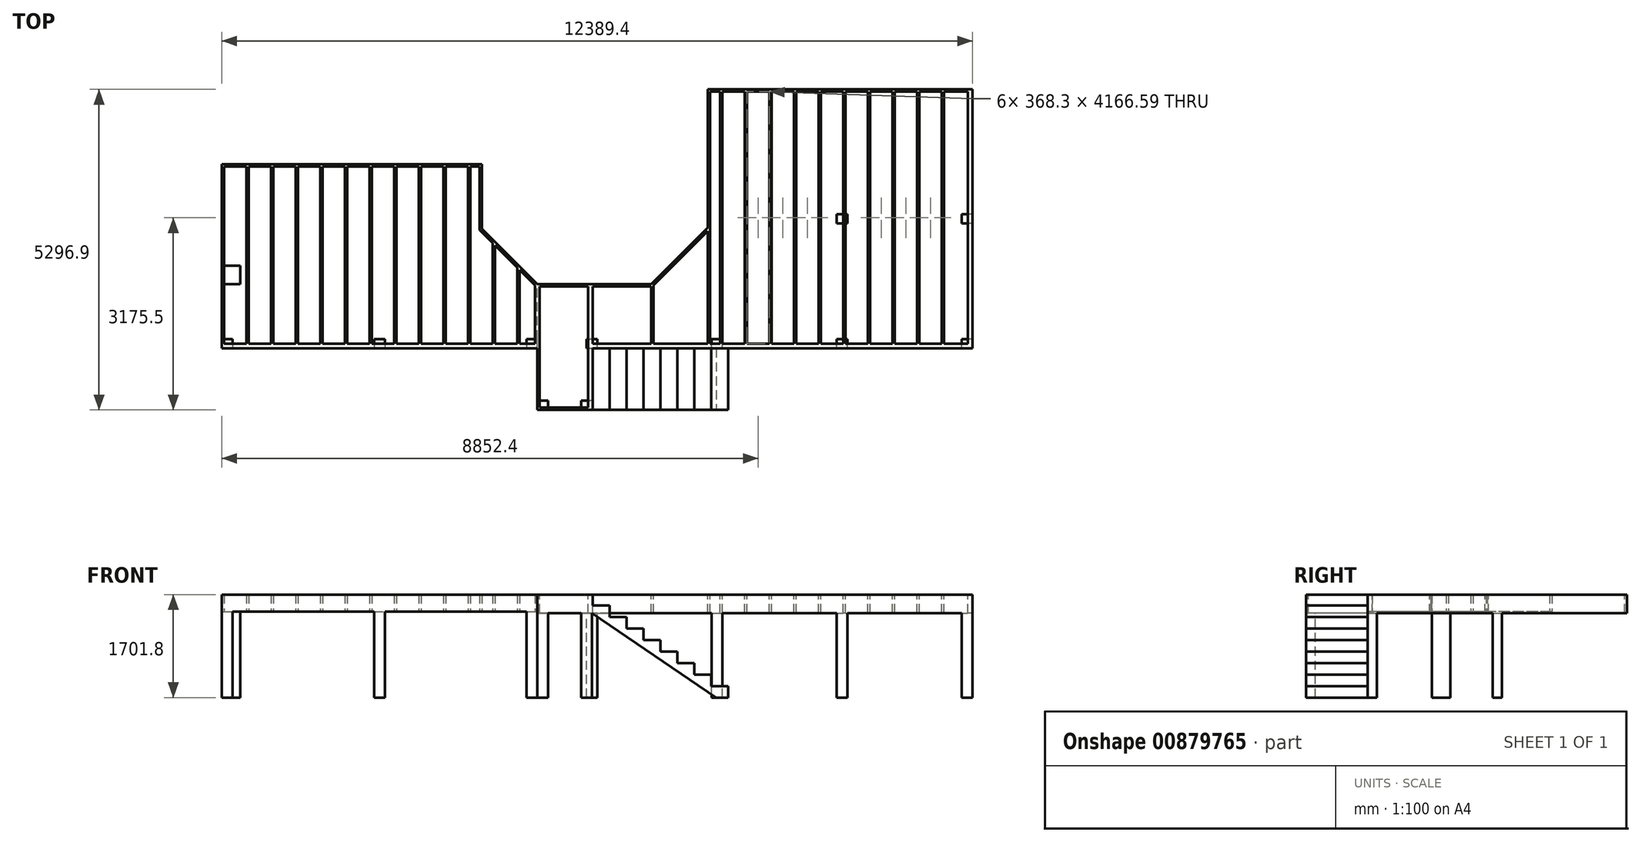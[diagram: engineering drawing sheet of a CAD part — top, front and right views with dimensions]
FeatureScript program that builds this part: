
annotation { "Feature Type Name" : "Feature", "Feature Type Description" : "" }
export const myFeature = defineFeature(function(context is Context, id is Id, definition is map)
    precondition{}
    {
        {
            var Q0;
            Q0=qCreatedBy(makeId("Top.planeOp"),FACE);
            var sketch = newSketch(context, id + "F0", { "sketchPlane" : qUnion([Q0])});
            skLineSegment(sketch, "E0.bottom", {"start": v(0, -1676.4) * mm, "end": v(304.8, -1676.4) * mm});
            skLineSegment(sketch, "E0.top", {"start": v(0, -1981.2) * mm, "end": v(304.8, -1981.2) * mm});
            skLineSegment(sketch, "E0.left", {"start": v(0, -1676.4) * mm, "end": v(0, -1981.2) * mm});
            skLineSegment(sketch, "E0.right", {"start": v(304.8, -1676.4) * mm, "end": v(304.8, -1981.2) * mm});
            skLineSegment(sketch, "E1.bottom", {"start": v(0, -2889.75) * mm, "end": v(177.8, -2889.75) * mm});
            skLineSegment(sketch, "E1.top", {"start": v(0, -3042.15) * mm, "end": v(177.8, -3042.15) * mm});
            skLineSegment(sketch, "E1.left", {"start": v(0, -2889.75) * mm, "end": v(0, -3042.15) * mm});
            skLineSegment(sketch, "E1.right", {"start": v(177.8, -2889.75) * mm, "end": v(177.8, -3042.15) * mm});
            skLineSegment(sketch, "E2.bottom", {"start": v(2514.6, -2889.75) * mm, "end": v(2692.4, -2889.75) * mm});
            skLineSegment(sketch, "E2.top", {"start": v(2514.6, -3042.15) * mm, "end": v(2692.4, -3042.15) * mm});
            skLineSegment(sketch, "E2.left", {"start": v(2514.6, -2889.75) * mm, "end": v(2514.6, -3042.15) * mm});
            skLineSegment(sketch, "E2.right", {"start": v(2692.4, -2889.75) * mm, "end": v(2692.4, -3042.15) * mm});
            skLineSegment(sketch, "E3.bottom", {"start": v(5029.2, -2889.75) * mm, "end": v(5207, -2889.75) * mm});
            skLineSegment(sketch, "E3.top", {"start": v(5029.2, -3042.15) * mm, "end": v(5207, -3042.15) * mm});
            skLineSegment(sketch, "E3.left", {"start": v(5029.2, -2889.75) * mm, "end": v(5029.2, -3042.15) * mm});
            skLineSegment(sketch, "E3.right", {"start": v(5207, -2889.75) * mm, "end": v(5207, -3042.15) * mm});
            skLineSegment(sketch, "E4", {"start": v(0, 0) * mm, "end": v(4292.6, 0) * mm, "construction": true});
            skLineSegment(sketch, "E5", {"start": v(4292.6, 0) * mm, "end": v(4292.6, -1066.8) * mm, "construction": true});
            skLineSegment(sketch, "E6", {"start": v(4292.6, -1066.8) * mm, "end": v(5226.55, -2000.75) * mm, "construction": true});
            skLineSegment(sketch, "E7", {"start": v(5226.55, -2000.75) * mm, "end": v(7106.15, -2000.75) * mm, "construction": true});
            skSolve(sketch);
        }
        {
            var Q0;
            Q0=qSketchRegion(id+"F0",true);
            extrude(context, id + "F1", {"entities" : qUnion([Q0]), "depth" : 1422.4 * mm, "offsetDistance" : 25.4 * mm});
        }
        {
            var Q0;
            Q0=makeQuery(id+"F1.opExtrude","CAP_FACE",FACE,{"disambiguationData":[OSD([sQuery(id+"F0.wireOp",EDGE,"E0.bottom"),sQuery(id+"F0.wireOp",EDGE,"E0.top"),sQuery(id+"F0.wireOp",EDGE,"E0.left"),sQuery(id+"F0.wireOp",EDGE,"E0.right")])],"isStart":false});
            var sketch = newSketch(context, id + "F2", { "sketchPlane" : qUnion([Q0])});
            skLineSegment(sketch, "E8.0", {"start": v(0, 0) * mm, "end": v(4292.6, 0) * mm});
            skLineSegment(sketch, "E9.0", {"start": v(4292.6, 0) * mm, "end": v(4292.6, -1066.8) * mm});
            skLineSegment(sketch, "E9.1", {"start": v(4292.6, -1066.8) * mm, "end": v(5207, -1981.2) * mm});
            skLineSegment(sketch, "E10", {"start": v(0, 0) * mm, "end": v(0, -3042.15) * mm});
            skLineSegment(sketch, "E11", {"start": v(0, -3042.15) * mm, "end": v(5207, -3042.15) * mm});
            skLineSegment(sketch, "E12", {"start": v(5207, -3042.15) * mm, "end": v(5207, -1981.2) * mm});
            skPoint(sketch, "E13.orphan", {"position": v(5226.55, -2000.75) * mm});
            skLineSegment(sketch, "E14.0", {"start": v(4254.5, -38.1) * mm, "end": v(4254.5, -1082.58) * mm});
            skLineSegment(sketch, "E14.1", {"start": v(5168.9, -3004.05) * mm, "end": v(5168.9, -1996.98) * mm});
            skLineSegment(sketch, "E14.2", {"start": v(38.1, -3004.05) * mm, "end": v(5168.9, -3004.05) * mm});
            skLineSegment(sketch, "E14.3", {"start": v(4254.5, -1082.58) * mm, "end": v(5168.9, -1996.98) * mm});
            skLineSegment(sketch, "E14.4", {"start": v(38.1, -38.1) * mm, "end": v(38.1, -3004.05) * mm});
            skLineSegment(sketch, "E14.5", {"start": v(38.1, -38.1) * mm, "end": v(4254.5, -38.1) * mm});
            skSolve(sketch);
        }
        {
            var Q0;
            Q0=qSketchRegion(id+"F2",true);
            extrude(context, id + "F3", {"entities" : qUnion([Q0]), "operationType" : NewBodyOperationType.ADD, "depth" : 279.4 * mm, "offsetDistance" : 25.4 * mm});
        }
        {
            var Q0;
            Q0=makeQuery(id+"F1.opExtrude","CAP_FACE",FACE,{"disambiguationData":[OSD([sQuery(id+"F0.wireOp",EDGE,"E1.bottom"),sQuery(id+"F0.wireOp",EDGE,"E1.top"),sQuery(id+"F0.wireOp",EDGE,"E1.left"),sQuery(id+"F0.wireOp",EDGE,"E1.right")])],"isStart":false});
            var sketch = newSketch(context, id + "F4", { "sketchPlane" : qUnion([Q0])});
            skPoint(sketch, "E15.oppositeSnap0", {"position": v(38.1, -2965.95) * mm});
            skLineSegment(sketch, "E15.bottom", {"start": v(38.1, -3004.05) * mm, "end": v(5168.9, -3004.05) * mm});
            skLineSegment(sketch, "E15.top", {"start": v(38.1, -2965.95) * mm, "end": v(5168.9, -2965.95) * mm});
            skLineSegment(sketch, "E15.left", {"start": v(38.1, -3004.05) * mm, "end": v(38.1, -2965.95) * mm});
            skLineSegment(sketch, "E15.right", {"start": v(5168.9, -3004.05) * mm, "end": v(5168.9, -2965.95) * mm});
            skSolve(sketch);
        }
        {
            var Q0;
            Q0=qSketchRegion(id+"F4",true);
            var Q1;
            Q1=makeQuery(id+"F3.opExtrude","CAP_FACE",FACE,{"disambiguationData":[OSD([sQuery(id+"F2.wireOp",EDGE,"E8.0"),sQuery(id+"F2.wireOp",EDGE,"E9.0"),sQuery(id+"F2.wireOp",EDGE,"E9.1"),sQuery(id+"F2.wireOp",EDGE,"E10"),sQuery(id+"F2.wireOp",EDGE,"E11"),sQuery(id+"F2.wireOp",EDGE,"E12"),sQuery(id+"F2.wireOp",EDGE,"E14.0"),sQuery(id+"F2.wireOp",EDGE,"E14.1"),sQuery(id+"F2.wireOp",EDGE,"E14.2"),sQuery(id+"F2.wireOp",EDGE,"E14.3"),sQuery(id+"F2.wireOp",EDGE,"E14.4"),sQuery(id+"F2.wireOp",EDGE,"E14.5")])],"isStart":false});
            extrude(context, id + "F5", {"entities" : qUnion([Q0]), "operationType" : NewBodyOperationType.ADD, "endBound" : BoundingType.UP_TO_SURFACE, "depth" : 25.4 * mm, "endBoundEntityFace" : qUnion([Q1]), "offsetDistance" : 25.4 * mm});
        }
        {
            var Q0;
            Q0=makeQuery(id+"F1.opExtrude","CAP_FACE",FACE,{"disambiguationData":[OSD([sQuery(id+"F0.wireOp",EDGE,"E0.bottom"),sQuery(id+"F0.wireOp",EDGE,"E0.top"),sQuery(id+"F0.wireOp",EDGE,"E0.left"),sQuery(id+"F0.wireOp",EDGE,"E0.right")])],"isStart":false});
            var sketch = newSketch(context, id + "F6", { "sketchPlane" : qUnion([Q0])});
            skLineSegment(sketch, "E16.bottom", {"start": v(406.4, -38.1) * mm, "end": v(444.5, -38.1) * mm});
            skLineSegment(sketch, "E16.top", {"start": v(406.4, -2965.95) * mm, "end": v(444.5, -2965.95) * mm});
            skLineSegment(sketch, "E16.left", {"start": v(406.4, -38.1) * mm, "end": v(406.4, -2965.95) * mm});
            skLineSegment(sketch, "E16.right", {"start": v(444.5, -38.1) * mm, "end": v(444.5, -2965.95) * mm});
            skLineSegment(sketch, "E17.1.0.0", {"start": v(850.9, -38.1) * mm, "end": v(850.9, -2965.95) * mm});
            skLineSegment(sketch, "E17.1.0.1", {"start": v(812.8, -38.1) * mm, "end": v(812.8, -2965.95) * mm});
            skLineSegment(sketch, "E17.1.0.2", {"start": v(812.8, -38.1) * mm, "end": v(850.9, -38.1) * mm});
            skLineSegment(sketch, "E17.1.0.3", {"start": v(812.8, -2965.95) * mm, "end": v(850.9, -2965.95) * mm});
            skLineSegment(sketch, "E17.2.0.0", {"start": v(1257.3, -38.1) * mm, "end": v(1257.3, -2965.95) * mm});
            skLineSegment(sketch, "E17.2.0.1", {"start": v(1219.2, -38.1) * mm, "end": v(1219.2, -2965.95) * mm});
            skLineSegment(sketch, "E17.2.0.2", {"start": v(1219.2, -38.1) * mm, "end": v(1257.3, -38.1) * mm});
            skLineSegment(sketch, "E17.2.0.3", {"start": v(1219.2, -2965.95) * mm, "end": v(1257.3, -2965.95) * mm});
            skLineSegment(sketch, "E17.3.0.0", {"start": v(1663.7, -38.1) * mm, "end": v(1663.7, -2965.95) * mm});
            skLineSegment(sketch, "E17.3.0.1", {"start": v(1625.6, -38.1) * mm, "end": v(1625.6, -2965.95) * mm});
            skLineSegment(sketch, "E17.3.0.2", {"start": v(1625.6, -38.1) * mm, "end": v(1663.7, -38.1) * mm});
            skLineSegment(sketch, "E17.3.0.3", {"start": v(1625.6, -2965.95) * mm, "end": v(1663.7, -2965.95) * mm});
            skLineSegment(sketch, "E17.4.0.0", {"start": v(2070.1, -38.1) * mm, "end": v(2070.1, -2965.95) * mm});
            skLineSegment(sketch, "E17.4.0.1", {"start": v(2032, -38.1) * mm, "end": v(2032, -2965.95) * mm});
            skLineSegment(sketch, "E17.4.0.2", {"start": v(2032, -38.1) * mm, "end": v(2070.1, -38.1) * mm});
            skLineSegment(sketch, "E17.4.0.3", {"start": v(2032, -2965.95) * mm, "end": v(2070.1, -2965.95) * mm});
            skLineSegment(sketch, "E17.5.0.0", {"start": v(2476.5, -38.1) * mm, "end": v(2476.5, -2965.95) * mm});
            skLineSegment(sketch, "E17.5.0.1", {"start": v(2438.4, -38.1) * mm, "end": v(2438.4, -2965.95) * mm});
            skLineSegment(sketch, "E17.5.0.2", {"start": v(2438.4, -38.1) * mm, "end": v(2476.5, -38.1) * mm});
            skLineSegment(sketch, "E17.5.0.3", {"start": v(2438.4, -2965.95) * mm, "end": v(2476.5, -2965.95) * mm});
            skLineSegment(sketch, "E17.6.0.0", {"start": v(2882.9, -38.1) * mm, "end": v(2882.9, -2965.95) * mm});
            skLineSegment(sketch, "E17.6.0.1", {"start": v(2844.8, -38.1) * mm, "end": v(2844.8, -2965.95) * mm});
            skLineSegment(sketch, "E17.6.0.2", {"start": v(2844.8, -38.1) * mm, "end": v(2882.9, -38.1) * mm});
            skLineSegment(sketch, "E17.6.0.3", {"start": v(2844.8, -2965.95) * mm, "end": v(2882.9, -2965.95) * mm});
            skLineSegment(sketch, "E17.7.0.0", {"start": v(3289.3, -38.1) * mm, "end": v(3289.3, -2965.95) * mm});
            skLineSegment(sketch, "E17.7.0.1", {"start": v(3251.2, -38.1) * mm, "end": v(3251.2, -2965.95) * mm});
            skLineSegment(sketch, "E17.7.0.2", {"start": v(3251.2, -38.1) * mm, "end": v(3289.3, -38.1) * mm});
            skLineSegment(sketch, "E17.7.0.3", {"start": v(3251.2, -2965.95) * mm, "end": v(3289.3, -2965.95) * mm});
            skLineSegment(sketch, "E17.8.0.0", {"start": v(3695.7, -38.1) * mm, "end": v(3695.7, -2965.95) * mm});
            skLineSegment(sketch, "E17.8.0.1", {"start": v(3657.6, -38.1) * mm, "end": v(3657.6, -2965.95) * mm});
            skLineSegment(sketch, "E17.8.0.2", {"start": v(3657.6, -38.1) * mm, "end": v(3695.7, -38.1) * mm});
            skLineSegment(sketch, "E17.8.0.3", {"start": v(3657.6, -2965.95) * mm, "end": v(3695.7, -2965.95) * mm});
            skLineSegment(sketch, "E17.9.0.0", {"start": v(4102.1, -38.1) * mm, "end": v(4102.1, -2965.95) * mm});
            skLineSegment(sketch, "E17.9.0.1", {"start": v(4064, -38.1) * mm, "end": v(4064, -2965.95) * mm});
            skLineSegment(sketch, "E17.9.0.2", {"start": v(4064, -38.1) * mm, "end": v(4102.1, -38.1) * mm});
            skLineSegment(sketch, "E17.9.0.3", {"start": v(4064, -2965.95) * mm, "end": v(4102.1, -2965.95) * mm});
            skLineSegment(sketch, "E17.direction1", {"start": v(406.4, -2965.95) * mm, "end": v(812.8, -2965.95) * mm, "construction": true});
            skLineSegment(sketch, "E18.top", {"start": v(4470.4, -2965.95) * mm, "end": v(4508.5, -2965.95) * mm});
            skLineSegment(sketch, "E18.left", {"start": v(4470.4, -1298.48) * mm, "end": v(4470.4, -2965.95) * mm});
            skLineSegment(sketch, "E18.right", {"start": v(4508.5, -1336.58) * mm, "end": v(4508.5, -2965.95) * mm});
            skLineSegment(sketch, "E19.top", {"start": v(4876.8, -2965.95) * mm, "end": v(4914.9, -2965.95) * mm});
            skLineSegment(sketch, "E19.left", {"start": v(4876.8, -1704.88) * mm, "end": v(4876.8, -2965.95) * mm});
            skLineSegment(sketch, "E19.right", {"start": v(4914.9, -1742.98) * mm, "end": v(4914.9, -2965.95) * mm});
            skLineSegment(sketch, "E20", {"start": v(4470.4, -1298.48) * mm, "end": v(4508.5, -1336.58) * mm});
            skLineSegment(sketch, "E21.trimOffspring", {"start": v(4876.8, -1704.88) * mm, "end": v(4914.9, -1742.98) * mm});
            skSolve(sketch);
        }
        {
            var Q0;
            Q0=qSketchRegion(id+"F6",true);
            var Q1;
            {var subQ0=sQuery(id+"F2.wireOp",EDGE,"E14.5");var subQ1=sQuery(id+"F2.wireOp",EDGE,"E14.4");var subQ2=sQuery(id+"F2.wireOp",EDGE,"E14.3");var subQ3=sQuery(id+"F2.wireOp",EDGE,"E14.2");var subQ4=sQuery(id+"F2.wireOp",EDGE,"E14.1");var subQ5=sQuery(id+"F2.wireOp",EDGE,"E14.0");var subQ6=sQuery(id+"F2.wireOp",EDGE,"E12");var subQ7=sQuery(id+"F2.wireOp",EDGE,"E11");var subQ8=sQuery(id+"F2.wireOp",EDGE,"E10");var subQ9=sQuery(id+"F2.wireOp",EDGE,"E9.1");var subQ10=sQuery(id+"F2.wireOp",EDGE,"E9.0");var subQ11=sQuery(id+"F2.wireOp",EDGE,"E8.0");Q1=makeQuery(id+"F5.boolean.opBoolean","MERGE",FACE,{"derivedFrom":[makeQuery(id+"F3.opExtrude","CAP_FACE",FACE,{"disambiguationData":[OSD([subQ11,subQ10,subQ9,subQ8,subQ7,subQ6,subQ5,subQ4,subQ3,subQ2,subQ1,subQ0])],"isStart":false}),makeQuery(id+"F5.opExtrude","CAP_FACE",FACE,{"disambiguationData":[OSD([subQ11,subQ10,subQ9,subQ8,subQ7,subQ6,subQ5,subQ4,subQ3,subQ2,subQ1,subQ0])],"isStart":false})]});}
            extrude(context, id + "F7", {"entities" : qUnion([Q0]), "operationType" : NewBodyOperationType.ADD, "endBound" : BoundingType.UP_TO_SURFACE, "depth" : 25.4 * mm, "endBoundEntityFace" : qUnion([Q1]), "offsetDistance" : 25.4 * mm});
        }
        {
            var Q0;
            Q0=makeQuery(id+"F7.boolean.opBoolean","MERGE",FACE,{"derivedFrom":[makeQuery(id+"F5.boolean.opBoolean","MERGE",FACE,{"derivedFrom":[makeQuery(id+"F3.opExtrude","CAP_FACE",FACE,{"disambiguationData":[OSD([sQuery(id+"F2.wireOp",EDGE,"E8.0"),sQuery(id+"F2.wireOp",EDGE,"E9.0"),sQuery(id+"F2.wireOp",EDGE,"E9.1"),sQuery(id+"F2.wireOp",EDGE,"E10"),sQuery(id+"F2.wireOp",EDGE,"E11"),sQuery(id+"F2.wireOp",EDGE,"E12"),sQuery(id+"F2.wireOp",EDGE,"E14.0"),sQuery(id+"F2.wireOp",EDGE,"E14.1"),sQuery(id+"F2.wireOp",EDGE,"E14.2"),sQuery(id+"F2.wireOp",EDGE,"E14.3"),sQuery(id+"F2.wireOp",EDGE,"E14.4"),sQuery(id+"F2.wireOp",EDGE,"E14.5")])],"isStart":false}),makeQuery(id+"F5.opExtrude","CAP_FACE",FACE,{"disambiguationData":[OSD([sQuery(id+"F4.wireOp",EDGE,"E15.bottom"),sQuery(id+"F4.wireOp",EDGE,"E15.top"),sQuery(id+"F4.wireOp",EDGE,"E15.left"),sQuery(id+"F4.wireOp",EDGE,"E15.right")])],"isStart":false})]}),makeQuery(id+"F7.opExtrude","CAP_FACE",FACE,{"disambiguationData":[OSD([sQuery(id+"F6.wireOp",EDGE,"E16.bottom"),sQuery(id+"F6.wireOp",EDGE,"E16.top"),sQuery(id+"F6.wireOp",EDGE,"E16.left"),sQuery(id+"F6.wireOp",EDGE,"E16.right")])],"isStart":false}),makeQuery(id+"F7.opExtrude","CAP_FACE",FACE,{"disambiguationData":[OSD([sQuery(id+"F6.wireOp",EDGE,"E17.1.0.0"),sQuery(id+"F6.wireOp",EDGE,"E17.1.0.1"),sQuery(id+"F6.wireOp",EDGE,"E17.1.0.2"),sQuery(id+"F6.wireOp",EDGE,"E17.1.0.3")])],"isStart":false}),makeQuery(id+"F7.opExtrude","CAP_FACE",FACE,{"disambiguationData":[OSD([sQuery(id+"F6.wireOp",EDGE,"E17.2.0.0"),sQuery(id+"F6.wireOp",EDGE,"E17.2.0.1"),sQuery(id+"F6.wireOp",EDGE,"E17.2.0.2"),sQuery(id+"F6.wireOp",EDGE,"E17.2.0.3")])],"isStart":false}),makeQuery(id+"F7.opExtrude","CAP_FACE",FACE,{"disambiguationData":[OSD([sQuery(id+"F6.wireOp",EDGE,"E17.3.0.0"),sQuery(id+"F6.wireOp",EDGE,"E17.3.0.1"),sQuery(id+"F6.wireOp",EDGE,"E17.3.0.2"),sQuery(id+"F6.wireOp",EDGE,"E17.3.0.3")])],"isStart":false}),makeQuery(id+"F7.opExtrude","CAP_FACE",FACE,{"disambiguationData":[OSD([sQuery(id+"F6.wireOp",EDGE,"E17.4.0.0"),sQuery(id+"F6.wireOp",EDGE,"E17.4.0.1"),sQuery(id+"F6.wireOp",EDGE,"E17.4.0.2"),sQuery(id+"F6.wireOp",EDGE,"E17.4.0.3")])],"isStart":false}),makeQuery(id+"F7.opExtrude","CAP_FACE",FACE,{"disambiguationData":[OSD([sQuery(id+"F6.wireOp",EDGE,"E17.5.0.0"),sQuery(id+"F6.wireOp",EDGE,"E17.5.0.1"),sQuery(id+"F6.wireOp",EDGE,"E17.5.0.2"),sQuery(id+"F6.wireOp",EDGE,"E17.5.0.3")])],"isStart":false}),makeQuery(id+"F7.opExtrude","CAP_FACE",FACE,{"disambiguationData":[OSD([sQuery(id+"F6.wireOp",EDGE,"E17.6.0.0"),sQuery(id+"F6.wireOp",EDGE,"E17.6.0.1"),sQuery(id+"F6.wireOp",EDGE,"E17.6.0.2"),sQuery(id+"F6.wireOp",EDGE,"E17.6.0.3")])],"isStart":false}),makeQuery(id+"F7.opExtrude","CAP_FACE",FACE,{"disambiguationData":[OSD([sQuery(id+"F6.wireOp",EDGE,"E17.7.0.0"),sQuery(id+"F6.wireOp",EDGE,"E17.7.0.1"),sQuery(id+"F6.wireOp",EDGE,"E17.7.0.2"),sQuery(id+"F6.wireOp",EDGE,"E17.7.0.3")])],"isStart":false}),makeQuery(id+"F7.opExtrude","CAP_FACE",FACE,{"disambiguationData":[OSD([sQuery(id+"F6.wireOp",EDGE,"E17.8.0.0"),sQuery(id+"F6.wireOp",EDGE,"E17.8.0.1"),sQuery(id+"F6.wireOp",EDGE,"E17.8.0.2"),sQuery(id+"F6.wireOp",EDGE,"E17.8.0.3")])],"isStart":false}),makeQuery(id+"F7.opExtrude","CAP_FACE",FACE,{"disambiguationData":[OSD([sQuery(id+"F6.wireOp",EDGE,"E17.9.0.0"),sQuery(id+"F6.wireOp",EDGE,"E17.9.0.1"),sQuery(id+"F6.wireOp",EDGE,"E17.9.0.2"),sQuery(id+"F6.wireOp",EDGE,"E17.9.0.3")])],"isStart":false}),makeQuery(id+"F7.opExtrude","CAP_FACE",FACE,{"disambiguationData":[OSD([sQuery(id+"F6.wireOp",EDGE,"E18.top"),sQuery(id+"F6.wireOp",EDGE,"E18.left"),sQuery(id+"F6.wireOp",EDGE,"E18.right"),sQuery(id+"F6.wireOp",EDGE,"E20")])],"isStart":false}),makeQuery(id+"F7.opExtrude","CAP_FACE",FACE,{"disambiguationData":[OSD([sQuery(id+"F6.wireOp",EDGE,"E19.top"),sQuery(id+"F6.wireOp",EDGE,"E19.left"),sQuery(id+"F6.wireOp",EDGE,"E19.right"),sQuery(id+"F6.wireOp",EDGE,"E21.trimOffspring")])],"isStart":false})]});
            var sketch = newSketch(context, id + "F8", { "sketchPlane" : qUnion([Q0])});
            skLineSegment(sketch, "E22", {"start": v(5207, -1981.2) * mm, "end": v(5207, -3042.15) * mm});
            skLineSegment(sketch, "E23", {"start": v(5207, -1981.2) * mm, "end": v(7086.6, -1981.2) * mm});
            skLineSegment(sketch, "E24", {"start": v(7086.6, -1981.2) * mm, "end": v(8020.55, -1047.25) * mm});
            skLineSegment(sketch, "E25", {"start": v(8020.55, -1047.25) * mm, "end": v(8020.55, 1238.75) * mm});
            skLineSegment(sketch, "E26", {"start": v(8020.55, 1238.75) * mm, "end": v(12389.35, 1238.75) * mm});
            skLineSegment(sketch, "E27", {"start": v(12389.35, 1238.75) * mm, "end": v(12389.35, -3042.15) * mm});
            skLineSegment(sketch, "E28", {"start": v(5207, -3042.15) * mm, "end": v(12389.35, -3042.15) * mm});
            skSolve(sketch);
        }
        {
            var Q0;
            Q0=qSketchRegion(id+"F8",true);
            extrude(context, id + "F9", {"entities" : qUnion([Q0]), "operationType" : NewBodyOperationType.ADD, "oppositeDirection" : true, "depth" : 304.8 * mm, "offsetDistance" : 25.4 * mm});
        }
        {
            var Q0;
            Q0=makeQuery(id+"F9.boolean.opBoolean","MERGE",FACE,{"derivedFrom":[makeQuery(id+"F7.boolean.opBoolean","MERGE",FACE,{"derivedFrom":[makeQuery(id+"F5.boolean.opBoolean","MERGE",FACE,{"derivedFrom":[makeQuery(id+"F3.opExtrude","CAP_FACE",FACE,{"disambiguationData":[OSD([sQuery(id+"F2.wireOp",EDGE,"E8.0"),sQuery(id+"F2.wireOp",EDGE,"E9.0"),sQuery(id+"F2.wireOp",EDGE,"E9.1"),sQuery(id+"F2.wireOp",EDGE,"E10"),sQuery(id+"F2.wireOp",EDGE,"E11"),sQuery(id+"F2.wireOp",EDGE,"E12"),sQuery(id+"F2.wireOp",EDGE,"E14.0"),sQuery(id+"F2.wireOp",EDGE,"E14.1"),sQuery(id+"F2.wireOp",EDGE,"E14.2"),sQuery(id+"F2.wireOp",EDGE,"E14.3"),sQuery(id+"F2.wireOp",EDGE,"E14.4"),sQuery(id+"F2.wireOp",EDGE,"E14.5")])],"isStart":false}),makeQuery(id+"F5.opExtrude","CAP_FACE",FACE,{"disambiguationData":[OSD([sQuery(id+"F4.wireOp",EDGE,"E15.bottom"),sQuery(id+"F4.wireOp",EDGE,"E15.top"),sQuery(id+"F4.wireOp",EDGE,"E15.left"),sQuery(id+"F4.wireOp",EDGE,"E15.right")])],"isStart":false})]}),makeQuery(id+"F7.opExtrude","CAP_FACE",FACE,{"disambiguationData":[OSD([sQuery(id+"F6.wireOp",EDGE,"E16.bottom"),sQuery(id+"F6.wireOp",EDGE,"E16.top"),sQuery(id+"F6.wireOp",EDGE,"E16.left"),sQuery(id+"F6.wireOp",EDGE,"E16.right")])],"isStart":false}),makeQuery(id+"F7.opExtrude","CAP_FACE",FACE,{"disambiguationData":[OSD([sQuery(id+"F6.wireOp",EDGE,"E17.1.0.0"),sQuery(id+"F6.wireOp",EDGE,"E17.1.0.1"),sQuery(id+"F6.wireOp",EDGE,"E17.1.0.2"),sQuery(id+"F6.wireOp",EDGE,"E17.1.0.3")])],"isStart":false}),makeQuery(id+"F7.opExtrude","CAP_FACE",FACE,{"disambiguationData":[OSD([sQuery(id+"F6.wireOp",EDGE,"E17.2.0.0"),sQuery(id+"F6.wireOp",EDGE,"E17.2.0.1"),sQuery(id+"F6.wireOp",EDGE,"E17.2.0.2"),sQuery(id+"F6.wireOp",EDGE,"E17.2.0.3")])],"isStart":false}),makeQuery(id+"F7.opExtrude","CAP_FACE",FACE,{"disambiguationData":[OSD([sQuery(id+"F6.wireOp",EDGE,"E17.3.0.0"),sQuery(id+"F6.wireOp",EDGE,"E17.3.0.1"),sQuery(id+"F6.wireOp",EDGE,"E17.3.0.2"),sQuery(id+"F6.wireOp",EDGE,"E17.3.0.3")])],"isStart":false}),makeQuery(id+"F7.opExtrude","CAP_FACE",FACE,{"disambiguationData":[OSD([sQuery(id+"F6.wireOp",EDGE,"E17.4.0.0"),sQuery(id+"F6.wireOp",EDGE,"E17.4.0.1"),sQuery(id+"F6.wireOp",EDGE,"E17.4.0.2"),sQuery(id+"F6.wireOp",EDGE,"E17.4.0.3")])],"isStart":false}),makeQuery(id+"F7.opExtrude","CAP_FACE",FACE,{"disambiguationData":[OSD([sQuery(id+"F6.wireOp",EDGE,"E17.5.0.0"),sQuery(id+"F6.wireOp",EDGE,"E17.5.0.1"),sQuery(id+"F6.wireOp",EDGE,"E17.5.0.2"),sQuery(id+"F6.wireOp",EDGE,"E17.5.0.3")])],"isStart":false}),makeQuery(id+"F7.opExtrude","CAP_FACE",FACE,{"disambiguationData":[OSD([sQuery(id+"F6.wireOp",EDGE,"E17.6.0.0"),sQuery(id+"F6.wireOp",EDGE,"E17.6.0.1"),sQuery(id+"F6.wireOp",EDGE,"E17.6.0.2"),sQuery(id+"F6.wireOp",EDGE,"E17.6.0.3")])],"isStart":false}),makeQuery(id+"F7.opExtrude","CAP_FACE",FACE,{"disambiguationData":[OSD([sQuery(id+"F6.wireOp",EDGE,"E17.7.0.0"),sQuery(id+"F6.wireOp",EDGE,"E17.7.0.1"),sQuery(id+"F6.wireOp",EDGE,"E17.7.0.2"),sQuery(id+"F6.wireOp",EDGE,"E17.7.0.3")])],"isStart":false}),makeQuery(id+"F7.opExtrude","CAP_FACE",FACE,{"disambiguationData":[OSD([sQuery(id+"F6.wireOp",EDGE,"E17.8.0.0"),sQuery(id+"F6.wireOp",EDGE,"E17.8.0.1"),sQuery(id+"F6.wireOp",EDGE,"E17.8.0.2"),sQuery(id+"F6.wireOp",EDGE,"E17.8.0.3")])],"isStart":false}),makeQuery(id+"F7.opExtrude","CAP_FACE",FACE,{"disambiguationData":[OSD([sQuery(id+"F6.wireOp",EDGE,"E17.9.0.0"),sQuery(id+"F6.wireOp",EDGE,"E17.9.0.1"),sQuery(id+"F6.wireOp",EDGE,"E17.9.0.2"),sQuery(id+"F6.wireOp",EDGE,"E17.9.0.3")])],"isStart":false}),makeQuery(id+"F7.opExtrude","CAP_FACE",FACE,{"disambiguationData":[OSD([sQuery(id+"F6.wireOp",EDGE,"E18.top"),sQuery(id+"F6.wireOp",EDGE,"E18.left"),sQuery(id+"F6.wireOp",EDGE,"E18.right"),sQuery(id+"F6.wireOp",EDGE,"E20")])],"isStart":false}),makeQuery(id+"F7.opExtrude","CAP_FACE",FACE,{"disambiguationData":[OSD([sQuery(id+"F6.wireOp",EDGE,"E19.top"),sQuery(id+"F6.wireOp",EDGE,"E19.left"),sQuery(id+"F6.wireOp",EDGE,"E19.right"),sQuery(id+"F6.wireOp",EDGE,"E21.trimOffspring")])],"isStart":false})]}),makeQuery(id+"F9.opExtrude","CAP_FACE",FACE,{"disambiguationData":[OSD([sQuery(id+"F8.wireOp",EDGE,"E22"),sQuery(id+"F8.wireOp",EDGE,"E23"),sQuery(id+"F8.wireOp",EDGE,"E24"),sQuery(id+"F8.wireOp",EDGE,"E25"),sQuery(id+"F8.wireOp",EDGE,"E26"),sQuery(id+"F8.wireOp",EDGE,"E27"),sQuery(id+"F8.wireOp",EDGE,"E28")])],"isStart":true})]});
            var sketch = newSketch(context, id + "F10", { "sketchPlane" : qUnion([Q0])});
            skLineSegment(sketch, "E29.bottom", {"start": v(6121.4, -3042.15) * mm, "end": v(5207, -3042.15) * mm});
            skLineSegment(sketch, "E29.top", {"start": v(6121.4, -4058.15) * mm, "end": v(5207, -4058.15) * mm});
            skLineSegment(sketch, "E29.left", {"start": v(6121.4, -3042.15) * mm, "end": v(6121.4, -4058.15) * mm});
            skLineSegment(sketch, "E29.right", {"start": v(5207, -3042.15) * mm, "end": v(5207, -4058.15) * mm});
            skSolve(sketch);
        }
        {
            var Q0;
            Q0=qSketchRegion(id+"F10",true);
            var Q1;
            Q1=makeQuery(id+"F9.opExtrude","CAP_FACE",FACE,{"disambiguationData":[OSD([sQuery(id+"F8.wireOp",EDGE,"E22"),sQuery(id+"F8.wireOp",EDGE,"E23"),sQuery(id+"F8.wireOp",EDGE,"E24"),sQuery(id+"F8.wireOp",EDGE,"E25"),sQuery(id+"F8.wireOp",EDGE,"E26"),sQuery(id+"F8.wireOp",EDGE,"E27"),sQuery(id+"F8.wireOp",EDGE,"E28")])],"isStart":false});
            extrude(context, id + "F11", {"entities" : qUnion([Q0]), "operationType" : NewBodyOperationType.ADD, "endBound" : BoundingType.UP_TO_SURFACE, "oppositeDirection" : true, "depth" : 25.4 * mm, "endBoundEntityFace" : qUnion([Q1]), "offsetDistance" : 25.4 * mm});
        }
        {
            var Q0;
            Q0=makeQuery(id+"F11.opExtrude","SWEPT_FACE",FACE,{"disambiguationData":[OSD([sQuery(id+"F10.wireOp",EDGE,"E29.top")])]});
            var sketch = newSketch(context, id + "F12", { "sketchPlane" : qUnion([Q0])});
            skLineSegment(sketch, "E30", {"start": v(6121.4, 1701.8) * mm, "end": v(6121.4, 1524) * mm});
            skLineSegment(sketch, "E31", {"start": v(6121.4, 1524) * mm, "end": v(6400.8, 1524) * mm});
            skLineSegment(sketch, "E32", {"start": v(6400.8, 1524) * mm, "end": v(6400.8, 1333.5) * mm});
            skLineSegment(sketch, "E33", {"start": v(6400.8, 1333.5) * mm, "end": v(6680.2, 1333.5) * mm});
            skLineSegment(sketch, "E34", {"start": v(6680.2, 1333.5) * mm, "end": v(6680.2, 1143) * mm});
            skLineSegment(sketch, "E35", {"start": v(6680.2, 1143) * mm, "end": v(6959.6, 1143) * mm});
            skLineSegment(sketch, "E36", {"start": v(6959.6, 1143) * mm, "end": v(6959.6, 952.5) * mm});
            skLineSegment(sketch, "E37", {"start": v(6959.6, 952.5) * mm, "end": v(7239, 952.5) * mm});
            skLineSegment(sketch, "E38", {"start": v(7239, 952.5) * mm, "end": v(7239, 762) * mm});
            skLineSegment(sketch, "E39", {"start": v(7239, 762) * mm, "end": v(7518.4, 762) * mm});
            skLineSegment(sketch, "E40", {"start": v(7518.4, 762) * mm, "end": v(7518.4, 571.5) * mm});
            skLineSegment(sketch, "E41", {"start": v(7518.4, 571.5) * mm, "end": v(7797.8, 571.5) * mm});
            skLineSegment(sketch, "E42", {"start": v(7797.8, 571.5) * mm, "end": v(7797.8, 381) * mm});
            skLineSegment(sketch, "E43", {"start": v(7797.8, 381) * mm, "end": v(8077.2, 381) * mm});
            skLineSegment(sketch, "E44", {"start": v(8077.2, 381) * mm, "end": v(8077.2, 190.5) * mm});
            skLineSegment(sketch, "E45", {"start": v(8077.2, 190.5) * mm, "end": v(8356.6, 190.5) * mm});
            skLineSegment(sketch, "E46", {"start": v(8356.6, 190.5) * mm, "end": v(8356.6, 0) * mm});
            skLineSegment(sketch, "E47", {"start": v(6121.4, 1701.8) * mm, "end": v(5664.2, 1701.8) * mm});
            skLineSegment(sketch, "E48", {"start": v(5664.2, 1701.8) * mm, "end": v(8160.17, 0) * mm});
            skLineSegment(sketch, "E49", {"start": v(8160.17, 0) * mm, "end": v(8356.6, 0) * mm});
            skLineSegment(sketch, "E50", {"start": v(6680.2, 1333.5) * mm, "end": v(8077.2, 381) * mm, "construction": true});
            skSolve(sketch);
        }
        {
            var Q0;
            {var subQ0=sQuery(id+"F12.wireOp",EDGE,"E31");Q0=makeQuery(id+"F12.imprint","IMPRINT",FACE,{"disambiguationData":[TD([[makeQuery(id+"F12.imprint","IMPRINT",EDGE,{"derivedFrom":subQ0}),-1.0]])]});}
            var Q1;
            {var subQ0=sQuery(id+"F8.wireOp",EDGE,"E28");var subQ1=sQuery(id+"F8.wireOp",EDGE,"E27");var subQ7=sQuery(id+"F2.wireOp",EDGE,"E11");Q1=makeQuery(id+"F11.boolean.opBoolean","SPLIT",FACE,{"disambiguationData":[TD([makeQuery(id+"F9.opExtrude","SWEPT_FACE",FACE,{"disambiguationData":[OSD([subQ1])]})])],"derivedFrom":makeQuery(id+"F9.boolean.opBoolean","MERGE",FACE,{"derivedFrom":[makeQuery(id+"F3.boolean.opBoolean","MERGE",FACE,{"derivedFrom":[makeQuery(id+"F1.opExtrude","SWEPT_FACE",FACE,{"disambiguationData":[OSD([sQuery(id+"F0.wireOp",EDGE,"E1.top")])]}),makeQuery(id+"F1.opExtrude","SWEPT_FACE",FACE,{"disambiguationData":[OSD([sQuery(id+"F0.wireOp",EDGE,"E2.top")])]}),makeQuery(id+"F1.opExtrude","SWEPT_FACE",FACE,{"disambiguationData":[OSD([sQuery(id+"F0.wireOp",EDGE,"E3.top")])]}),makeQuery(id+"F3.opExtrude","SWEPT_FACE",FACE,{"disambiguationData":[OSD([subQ7])]})]}),makeQuery(id+"F9.opExtrude","SWEPT_FACE",FACE,{"disambiguationData":[OSD([subQ0])]})]})});}
            extrude(context, id + "F13", {"entities" : qUnion([Q0]), "operationType" : NewBodyOperationType.ADD, "endBound" : BoundingType.UP_TO_SURFACE, "oppositeDirection" : true, "depth" : 25.4 * mm, "endBoundEntityFace" : qUnion([Q1]), "offsetDistance" : 25.4 * mm});
        }
        {
            var Q0;
            Q0=makeQuery(id+"F11.boolean.opBoolean","MERGE",FACE,{"derivedFrom":[makeQuery(id+"F9.opExtrude","CAP_FACE",FACE,{"disambiguationData":[OSD([sQuery(id+"F8.wireOp",EDGE,"E22"),sQuery(id+"F8.wireOp",EDGE,"E23"),sQuery(id+"F8.wireOp",EDGE,"E24"),sQuery(id+"F8.wireOp",EDGE,"E25"),sQuery(id+"F8.wireOp",EDGE,"E26"),sQuery(id+"F8.wireOp",EDGE,"E27"),sQuery(id+"F8.wireOp",EDGE,"E28")])],"isStart":false}),makeQuery(id+"F11.opExtrude","CAP_FACE",FACE,{"disambiguationData":[OSD([sQuery(id+"F10.wireOp",EDGE,"E29.bottom"),sQuery(id+"F10.wireOp",EDGE,"E29.top"),sQuery(id+"F10.wireOp",EDGE,"E29.left"),sQuery(id+"F10.wireOp",EDGE,"E29.right")])],"isStart":false})]});
            var sketch = newSketch(context, id + "F14", { "sketchPlane" : qUnion([Q0])});
            skLineSegment(sketch, "E51.bottom", {"start": v(5384.8, 3905.75) * mm, "end": v(5207, 3905.75) * mm});
            skLineSegment(sketch, "E51.top", {"start": v(5384.8, 4058.15) * mm, "end": v(5207, 4058.15) * mm});
            skLineSegment(sketch, "E51.left", {"start": v(5384.8, 3905.75) * mm, "end": v(5384.8, 4058.15) * mm});
            skLineSegment(sketch, "E51.right", {"start": v(5207, 3905.75) * mm, "end": v(5207, 4058.15) * mm});
            skLineSegment(sketch, "E52.bottom", {"start": v(6111.24, 4058.15) * mm, "end": v(5933.44, 4058.15) * mm});
            skLineSegment(sketch, "E52.top", {"start": v(6111.24, 3905.75) * mm, "end": v(5933.44, 3905.75) * mm});
            skLineSegment(sketch, "E52.left", {"start": v(6111.24, 4058.15) * mm, "end": v(6111.24, 3905.75) * mm});
            skLineSegment(sketch, "E52.right", {"start": v(5933.44, 4058.15) * mm, "end": v(5933.44, 3905.75) * mm});
            skLineSegment(sketch, "E53.bottom", {"start": v(6200.14, 3042.15) * mm, "end": v(6022.34, 3042.15) * mm});
            skLineSegment(sketch, "E53.top", {"start": v(6200.14, 2889.75) * mm, "end": v(6022.34, 2889.75) * mm});
            skLineSegment(sketch, "E53.left", {"start": v(6200.14, 3042.15) * mm, "end": v(6200.14, 2889.75) * mm});
            skLineSegment(sketch, "E53.right", {"start": v(6022.34, 3042.15) * mm, "end": v(6022.34, 2889.75) * mm});
            skLineSegment(sketch, "E54.bottom", {"start": v(10326.28, 3042.15) * mm, "end": v(10148.48, 3042.15) * mm});
            skLineSegment(sketch, "E54.left", {"start": v(10326.28, 3042.15) * mm, "end": v(10326.28, 2889.75) * mm});
            skLineSegment(sketch, "E54.right", {"start": v(10148.48, 3042.15) * mm, "end": v(10148.48, 2889.75) * mm});
            skLineSegment(sketch, "E55.bottom", {"start": v(12389.35, 3042.15) * mm, "end": v(12211.55, 3042.15) * mm});
            skLineSegment(sketch, "E55.top", {"start": v(12389.35, 2889.75) * mm, "end": v(12211.55, 2889.75) * mm});
            skLineSegment(sketch, "E55.left", {"start": v(12389.35, 3042.15) * mm, "end": v(12389.35, 2889.75) * mm});
            skLineSegment(sketch, "E55.right", {"start": v(12211.55, 3042.15) * mm, "end": v(12211.55, 2889.75) * mm});
            skLineSegment(sketch, "E56.bottom", {"start": v(8085.4, 3042.15) * mm, "end": v(8263.2, 3042.15) * mm});
            skLineSegment(sketch, "E56.top", {"start": v(8085.4, 2889.75) * mm, "end": v(8263.2, 2889.75) * mm});
            skLineSegment(sketch, "E56.left", {"start": v(8085.4, 3042.15) * mm, "end": v(8085.4, 2889.75) * mm});
            skLineSegment(sketch, "E56.right", {"start": v(8263.2, 3042.15) * mm, "end": v(8263.2, 2889.75) * mm});
            skLineSegment(sketch, "E57.bottom", {"start": v(10326.28, 977.9) * mm, "end": v(10148.48, 977.9) * mm});
            skLineSegment(sketch, "E57.top", {"start": v(10326.28, 825.5) * mm, "end": v(10148.48, 825.5) * mm});
            skLineSegment(sketch, "E57.left", {"start": v(10148.48, 977.9) * mm, "end": v(10148.48, 825.5) * mm});
            skLineSegment(sketch, "E57.right", {"start": v(10326.28, 977.9) * mm, "end": v(10326.28, 825.5) * mm});
            skLineSegment(sketch, "E58.bottom", {"start": v(12389.35, 825.5) * mm, "end": v(12211.55, 825.5) * mm});
            skLineSegment(sketch, "E58.top", {"start": v(12389.35, 977.9) * mm, "end": v(12211.55, 977.9) * mm});
            skLineSegment(sketch, "E58.left", {"start": v(12389.35, 977.9) * mm, "end": v(12389.35, 825.5) * mm});
            skLineSegment(sketch, "E58.right", {"start": v(12211.55, 977.9) * mm, "end": v(12211.55, 825.5) * mm});
            skLineSegment(sketch, "E59", {"start": v(8263.2, 2889.75) * mm, "end": v(10148.48, 2889.75) * mm, "construction": true});
            skLineSegment(sketch, "E60", {"start": v(10326.28, 2889.75) * mm, "end": v(12211.55, 2889.75) * mm, "construction": true});
            skLineSegment(sketch, "E61", {"start": v(10148.48, 2889.75) * mm, "end": v(10326.28, 2889.75) * mm});
            skLineSegment(sketch, "E62", {"start": v(12211.55, 901.7) * mm, "end": v(12389.35, 901.7) * mm, "construction": true});
            skLineSegment(sketch, "E63", {"start": v(6200.14, 2889.75) * mm, "end": v(8085.4, 2889.75) * mm, "construction": true});
            skSolve(sketch);
        }
        {
            var Q0;
            Q0=qSketchRegion(id+"F14",true);
            var Q1;
            Q1=makeQuery(id+"F1.opExtrude","CAP_FACE",FACE,{"disambiguationData":[OSD([sQuery(id+"F0.wireOp",EDGE,"E3.bottom"),sQuery(id+"F0.wireOp",EDGE,"E3.top"),sQuery(id+"F0.wireOp",EDGE,"E3.left"),sQuery(id+"F0.wireOp",EDGE,"E3.right")])],"isStart":true});
            extrude(context, id + "F15", {"entities" : qUnion([Q0]), "operationType" : NewBodyOperationType.ADD, "endBound" : BoundingType.UP_TO_SURFACE, "depth" : 25.4 * mm, "endBoundEntityFace" : qUnion([Q1]), "offsetDistance" : 25.4 * mm});
        }
        {
            var Q0;
            Q0=makeQuery(id+"F11.boolean.opBoolean","MERGE",FACE,{"derivedFrom":[makeQuery(id+"F9.boolean.opBoolean","MERGE",FACE,{"derivedFrom":[makeQuery(id+"F7.boolean.opBoolean","MERGE",FACE,{"derivedFrom":[makeQuery(id+"F5.boolean.opBoolean","MERGE",FACE,{"derivedFrom":[makeQuery(id+"F3.opExtrude","CAP_FACE",FACE,{"disambiguationData":[OSD([sQuery(id+"F2.wireOp",EDGE,"E8.0"),sQuery(id+"F2.wireOp",EDGE,"E9.0"),sQuery(id+"F2.wireOp",EDGE,"E9.1"),sQuery(id+"F2.wireOp",EDGE,"E10"),sQuery(id+"F2.wireOp",EDGE,"E11"),sQuery(id+"F2.wireOp",EDGE,"E12"),sQuery(id+"F2.wireOp",EDGE,"E14.0"),sQuery(id+"F2.wireOp",EDGE,"E14.1"),sQuery(id+"F2.wireOp",EDGE,"E14.2"),sQuery(id+"F2.wireOp",EDGE,"E14.3"),sQuery(id+"F2.wireOp",EDGE,"E14.4"),sQuery(id+"F2.wireOp",EDGE,"E14.5")])],"isStart":false}),makeQuery(id+"F5.opExtrude","CAP_FACE",FACE,{"disambiguationData":[OSD([sQuery(id+"F4.wireOp",EDGE,"E15.bottom"),sQuery(id+"F4.wireOp",EDGE,"E15.top"),sQuery(id+"F4.wireOp",EDGE,"E15.left"),sQuery(id+"F4.wireOp",EDGE,"E15.right")])],"isStart":false})]}),makeQuery(id+"F7.opExtrude","CAP_FACE",FACE,{"disambiguationData":[OSD([sQuery(id+"F6.wireOp",EDGE,"E16.bottom"),sQuery(id+"F6.wireOp",EDGE,"E16.top"),sQuery(id+"F6.wireOp",EDGE,"E16.left"),sQuery(id+"F6.wireOp",EDGE,"E16.right")])],"isStart":false}),makeQuery(id+"F7.opExtrude","CAP_FACE",FACE,{"disambiguationData":[OSD([sQuery(id+"F6.wireOp",EDGE,"E17.1.0.0"),sQuery(id+"F6.wireOp",EDGE,"E17.1.0.1"),sQuery(id+"F6.wireOp",EDGE,"E17.1.0.2"),sQuery(id+"F6.wireOp",EDGE,"E17.1.0.3")])],"isStart":false}),makeQuery(id+"F7.opExtrude","CAP_FACE",FACE,{"disambiguationData":[OSD([sQuery(id+"F6.wireOp",EDGE,"E17.2.0.0"),sQuery(id+"F6.wireOp",EDGE,"E17.2.0.1"),sQuery(id+"F6.wireOp",EDGE,"E17.2.0.2"),sQuery(id+"F6.wireOp",EDGE,"E17.2.0.3")])],"isStart":false}),makeQuery(id+"F7.opExtrude","CAP_FACE",FACE,{"disambiguationData":[OSD([sQuery(id+"F6.wireOp",EDGE,"E17.3.0.0"),sQuery(id+"F6.wireOp",EDGE,"E17.3.0.1"),sQuery(id+"F6.wireOp",EDGE,"E17.3.0.2"),sQuery(id+"F6.wireOp",EDGE,"E17.3.0.3")])],"isStart":false}),makeQuery(id+"F7.opExtrude","CAP_FACE",FACE,{"disambiguationData":[OSD([sQuery(id+"F6.wireOp",EDGE,"E17.4.0.0"),sQuery(id+"F6.wireOp",EDGE,"E17.4.0.1"),sQuery(id+"F6.wireOp",EDGE,"E17.4.0.2"),sQuery(id+"F6.wireOp",EDGE,"E17.4.0.3")])],"isStart":false}),makeQuery(id+"F7.opExtrude","CAP_FACE",FACE,{"disambiguationData":[OSD([sQuery(id+"F6.wireOp",EDGE,"E17.5.0.0"),sQuery(id+"F6.wireOp",EDGE,"E17.5.0.1"),sQuery(id+"F6.wireOp",EDGE,"E17.5.0.2"),sQuery(id+"F6.wireOp",EDGE,"E17.5.0.3")])],"isStart":false}),makeQuery(id+"F7.opExtrude","CAP_FACE",FACE,{"disambiguationData":[OSD([sQuery(id+"F6.wireOp",EDGE,"E17.6.0.0"),sQuery(id+"F6.wireOp",EDGE,"E17.6.0.1"),sQuery(id+"F6.wireOp",EDGE,"E17.6.0.2"),sQuery(id+"F6.wireOp",EDGE,"E17.6.0.3")])],"isStart":false}),makeQuery(id+"F7.opExtrude","CAP_FACE",FACE,{"disambiguationData":[OSD([sQuery(id+"F6.wireOp",EDGE,"E17.7.0.0"),sQuery(id+"F6.wireOp",EDGE,"E17.7.0.1"),sQuery(id+"F6.wireOp",EDGE,"E17.7.0.2"),sQuery(id+"F6.wireOp",EDGE,"E17.7.0.3")])],"isStart":false}),makeQuery(id+"F7.opExtrude","CAP_FACE",FACE,{"disambiguationData":[OSD([sQuery(id+"F6.wireOp",EDGE,"E17.8.0.0"),sQuery(id+"F6.wireOp",EDGE,"E17.8.0.1"),sQuery(id+"F6.wireOp",EDGE,"E17.8.0.2"),sQuery(id+"F6.wireOp",EDGE,"E17.8.0.3")])],"isStart":false}),makeQuery(id+"F7.opExtrude","CAP_FACE",FACE,{"disambiguationData":[OSD([sQuery(id+"F6.wireOp",EDGE,"E17.9.0.0"),sQuery(id+"F6.wireOp",EDGE,"E17.9.0.1"),sQuery(id+"F6.wireOp",EDGE,"E17.9.0.2"),sQuery(id+"F6.wireOp",EDGE,"E17.9.0.3")])],"isStart":false}),makeQuery(id+"F7.opExtrude","CAP_FACE",FACE,{"disambiguationData":[OSD([sQuery(id+"F6.wireOp",EDGE,"E18.top"),sQuery(id+"F6.wireOp",EDGE,"E18.left"),sQuery(id+"F6.wireOp",EDGE,"E18.right"),sQuery(id+"F6.wireOp",EDGE,"E20")])],"isStart":false}),makeQuery(id+"F7.opExtrude","CAP_FACE",FACE,{"disambiguationData":[OSD([sQuery(id+"F6.wireOp",EDGE,"E19.top"),sQuery(id+"F6.wireOp",EDGE,"E19.left"),sQuery(id+"F6.wireOp",EDGE,"E19.right"),sQuery(id+"F6.wireOp",EDGE,"E21.trimOffspring")])],"isStart":false})]}),makeQuery(id+"F9.opExtrude","CAP_FACE",FACE,{"disambiguationData":[OSD([sQuery(id+"F8.wireOp",EDGE,"E22"),sQuery(id+"F8.wireOp",EDGE,"E23"),sQuery(id+"F8.wireOp",EDGE,"E24"),sQuery(id+"F8.wireOp",EDGE,"E25"),sQuery(id+"F8.wireOp",EDGE,"E26"),sQuery(id+"F8.wireOp",EDGE,"E27"),sQuery(id+"F8.wireOp",EDGE,"E28")])],"isStart":true})]}),makeQuery(id+"F11.opExtrude","CAP_FACE",FACE,{"disambiguationData":[OSD([sQuery(id+"F10.wireOp",EDGE,"E29.bottom"),sQuery(id+"F10.wireOp",EDGE,"E29.top"),sQuery(id+"F10.wireOp",EDGE,"E29.left"),sQuery(id+"F10.wireOp",EDGE,"E29.right")])],"isStart":true})]});
            var sketch = newSketch(context, id + "F16", { "sketchPlane" : qUnion([Q0])});
            skLineSegment(sketch, "E64.bottom", {"start": v(5245.1, -4020.05) * mm, "end": v(6045.2, -4020.05) * mm});
            skLineSegment(sketch, "E64.top", {"start": v(5245.1, -2019.3) * mm, "end": v(6045.2, -2019.3) * mm});
            skLineSegment(sketch, "E64.left", {"start": v(5245.1, -4020.05) * mm, "end": v(5245.1, -2019.3) * mm});
            skLineSegment(sketch, "E64.right", {"start": v(6045.2, -4020.05) * mm, "end": v(6045.2, -2019.3) * mm});
            skLineSegment(sketch, "E65.bottom", {"start": v(12313.15, -2965.95) * mm, "end": v(8058.65, -2965.95) * mm});
            skLineSegment(sketch, "E65.top", {"start": v(12313.15, 1200.65) * mm, "end": v(8058.65, 1200.65) * mm});
            skLineSegment(sketch, "E65.left", {"start": v(12313.15, -2965.95) * mm, "end": v(12313.15, 1200.65) * mm});
            skLineSegment(sketch, "E65.right", {"start": v(8058.65, -2965.95) * mm, "end": v(8058.65, 1200.65) * mm});
            skLineSegment(sketch, "E66.bottom", {"start": v(7086.6, -2019.3) * mm, "end": v(6121.4, -2019.3) * mm});
            skLineSegment(sketch, "E66.top", {"start": v(6121.4, -2965.95) * mm, "end": v(7086.6, -2965.95) * mm});
            skLineSegment(sketch, "E66.left", {"start": v(6121.4, -2019.3) * mm, "end": v(6121.4, -2965.95) * mm});
            skLineSegment(sketch, "E66.right", {"start": v(7086.6, -2019.3) * mm, "end": v(7086.6, -2965.95) * mm});
            skLineSegment(sketch, "E67", {"start": v(7124.7, -2965.95) * mm, "end": v(8020.55, -2965.95) * mm});
            skLineSegment(sketch, "E68", {"start": v(8020.55, -2965.95) * mm, "end": v(8020.55, -1101.13) * mm});
            skLineSegment(sketch, "E69", {"start": v(8020.55, -1101.13) * mm, "end": v(7124.7, -1996.98) * mm});
            skLineSegment(sketch, "E70", {"start": v(7124.7, -1996.98) * mm, "end": v(7124.7, -2965.95) * mm});
            skSolve(sketch);
        }
        {
            var Q0;
            Q0=qSketchRegion(id+"F16",true);
            var Q1;
            Q1=makeQuery(id+"F11.boolean.opBoolean","MERGE",FACE,{"derivedFrom":[makeQuery(id+"F9.opExtrude","CAP_FACE",FACE,{"disambiguationData":[OSD([sQuery(id+"F8.wireOp",EDGE,"E22"),sQuery(id+"F8.wireOp",EDGE,"E23"),sQuery(id+"F8.wireOp",EDGE,"E24"),sQuery(id+"F8.wireOp",EDGE,"E25"),sQuery(id+"F8.wireOp",EDGE,"E26"),sQuery(id+"F8.wireOp",EDGE,"E27"),sQuery(id+"F8.wireOp",EDGE,"E28")])],"isStart":false}),makeQuery(id+"F11.opExtrude","CAP_FACE",FACE,{"disambiguationData":[OSD([sQuery(id+"F10.wireOp",EDGE,"E29.bottom"),sQuery(id+"F10.wireOp",EDGE,"E29.top"),sQuery(id+"F10.wireOp",EDGE,"E29.left"),sQuery(id+"F10.wireOp",EDGE,"E29.right")])],"isStart":false})]});
            extrude(context, id + "F17", {"entities" : qUnion([Q0]), "operationType" : NewBodyOperationType.REMOVE, "endBound" : BoundingType.UP_TO_SURFACE, "oppositeDirection" : true, "depth" : 25.4 * mm, "endBoundEntityFace" : qUnion([Q1]), "offsetDistance" : 25.4 * mm});
        }
        {
            var Q0;
            Q0=makeQuery(id+"F11.boolean.opBoolean","MERGE",FACE,{"derivedFrom":[makeQuery(id+"F9.boolean.opBoolean","MERGE",FACE,{"derivedFrom":[makeQuery(id+"F7.boolean.opBoolean","MERGE",FACE,{"derivedFrom":[makeQuery(id+"F5.boolean.opBoolean","MERGE",FACE,{"derivedFrom":[makeQuery(id+"F3.opExtrude","CAP_FACE",FACE,{"disambiguationData":[OSD([sQuery(id+"F2.wireOp",EDGE,"E8.0"),sQuery(id+"F2.wireOp",EDGE,"E9.0"),sQuery(id+"F2.wireOp",EDGE,"E9.1"),sQuery(id+"F2.wireOp",EDGE,"E10"),sQuery(id+"F2.wireOp",EDGE,"E11"),sQuery(id+"F2.wireOp",EDGE,"E12"),sQuery(id+"F2.wireOp",EDGE,"E14.0"),sQuery(id+"F2.wireOp",EDGE,"E14.1"),sQuery(id+"F2.wireOp",EDGE,"E14.2"),sQuery(id+"F2.wireOp",EDGE,"E14.3"),sQuery(id+"F2.wireOp",EDGE,"E14.4"),sQuery(id+"F2.wireOp",EDGE,"E14.5")])],"isStart":false}),makeQuery(id+"F5.opExtrude","CAP_FACE",FACE,{"disambiguationData":[OSD([sQuery(id+"F4.wireOp",EDGE,"E15.bottom"),sQuery(id+"F4.wireOp",EDGE,"E15.top"),sQuery(id+"F4.wireOp",EDGE,"E15.left"),sQuery(id+"F4.wireOp",EDGE,"E15.right")])],"isStart":false})]}),makeQuery(id+"F7.opExtrude","CAP_FACE",FACE,{"disambiguationData":[OSD([sQuery(id+"F6.wireOp",EDGE,"E16.bottom"),sQuery(id+"F6.wireOp",EDGE,"E16.top"),sQuery(id+"F6.wireOp",EDGE,"E16.left"),sQuery(id+"F6.wireOp",EDGE,"E16.right")])],"isStart":false}),makeQuery(id+"F7.opExtrude","CAP_FACE",FACE,{"disambiguationData":[OSD([sQuery(id+"F6.wireOp",EDGE,"E17.1.0.0"),sQuery(id+"F6.wireOp",EDGE,"E17.1.0.1"),sQuery(id+"F6.wireOp",EDGE,"E17.1.0.2"),sQuery(id+"F6.wireOp",EDGE,"E17.1.0.3")])],"isStart":false}),makeQuery(id+"F7.opExtrude","CAP_FACE",FACE,{"disambiguationData":[OSD([sQuery(id+"F6.wireOp",EDGE,"E17.2.0.0"),sQuery(id+"F6.wireOp",EDGE,"E17.2.0.1"),sQuery(id+"F6.wireOp",EDGE,"E17.2.0.2"),sQuery(id+"F6.wireOp",EDGE,"E17.2.0.3")])],"isStart":false}),makeQuery(id+"F7.opExtrude","CAP_FACE",FACE,{"disambiguationData":[OSD([sQuery(id+"F6.wireOp",EDGE,"E17.3.0.0"),sQuery(id+"F6.wireOp",EDGE,"E17.3.0.1"),sQuery(id+"F6.wireOp",EDGE,"E17.3.0.2"),sQuery(id+"F6.wireOp",EDGE,"E17.3.0.3")])],"isStart":false}),makeQuery(id+"F7.opExtrude","CAP_FACE",FACE,{"disambiguationData":[OSD([sQuery(id+"F6.wireOp",EDGE,"E17.4.0.0"),sQuery(id+"F6.wireOp",EDGE,"E17.4.0.1"),sQuery(id+"F6.wireOp",EDGE,"E17.4.0.2"),sQuery(id+"F6.wireOp",EDGE,"E17.4.0.3")])],"isStart":false}),makeQuery(id+"F7.opExtrude","CAP_FACE",FACE,{"disambiguationData":[OSD([sQuery(id+"F6.wireOp",EDGE,"E17.5.0.0"),sQuery(id+"F6.wireOp",EDGE,"E17.5.0.1"),sQuery(id+"F6.wireOp",EDGE,"E17.5.0.2"),sQuery(id+"F6.wireOp",EDGE,"E17.5.0.3")])],"isStart":false}),makeQuery(id+"F7.opExtrude","CAP_FACE",FACE,{"disambiguationData":[OSD([sQuery(id+"F6.wireOp",EDGE,"E17.6.0.0"),sQuery(id+"F6.wireOp",EDGE,"E17.6.0.1"),sQuery(id+"F6.wireOp",EDGE,"E17.6.0.2"),sQuery(id+"F6.wireOp",EDGE,"E17.6.0.3")])],"isStart":false}),makeQuery(id+"F7.opExtrude","CAP_FACE",FACE,{"disambiguationData":[OSD([sQuery(id+"F6.wireOp",EDGE,"E17.7.0.0"),sQuery(id+"F6.wireOp",EDGE,"E17.7.0.1"),sQuery(id+"F6.wireOp",EDGE,"E17.7.0.2"),sQuery(id+"F6.wireOp",EDGE,"E17.7.0.3")])],"isStart":false}),makeQuery(id+"F7.opExtrude","CAP_FACE",FACE,{"disambiguationData":[OSD([sQuery(id+"F6.wireOp",EDGE,"E17.8.0.0"),sQuery(id+"F6.wireOp",EDGE,"E17.8.0.1"),sQuery(id+"F6.wireOp",EDGE,"E17.8.0.2"),sQuery(id+"F6.wireOp",EDGE,"E17.8.0.3")])],"isStart":false}),makeQuery(id+"F7.opExtrude","CAP_FACE",FACE,{"disambiguationData":[OSD([sQuery(id+"F6.wireOp",EDGE,"E17.9.0.0"),sQuery(id+"F6.wireOp",EDGE,"E17.9.0.1"),sQuery(id+"F6.wireOp",EDGE,"E17.9.0.2"),sQuery(id+"F6.wireOp",EDGE,"E17.9.0.3")])],"isStart":false}),makeQuery(id+"F7.opExtrude","CAP_FACE",FACE,{"disambiguationData":[OSD([sQuery(id+"F6.wireOp",EDGE,"E18.top"),sQuery(id+"F6.wireOp",EDGE,"E18.left"),sQuery(id+"F6.wireOp",EDGE,"E18.right"),sQuery(id+"F6.wireOp",EDGE,"E20")])],"isStart":false}),makeQuery(id+"F7.opExtrude","CAP_FACE",FACE,{"disambiguationData":[OSD([sQuery(id+"F6.wireOp",EDGE,"E19.top"),sQuery(id+"F6.wireOp",EDGE,"E19.left"),sQuery(id+"F6.wireOp",EDGE,"E19.right"),sQuery(id+"F6.wireOp",EDGE,"E21.trimOffspring")])],"isStart":false})]}),makeQuery(id+"F9.opExtrude","CAP_FACE",FACE,{"disambiguationData":[OSD([sQuery(id+"F8.wireOp",EDGE,"E22"),sQuery(id+"F8.wireOp",EDGE,"E23"),sQuery(id+"F8.wireOp",EDGE,"E24"),sQuery(id+"F8.wireOp",EDGE,"E25"),sQuery(id+"F8.wireOp",EDGE,"E26"),sQuery(id+"F8.wireOp",EDGE,"E27"),sQuery(id+"F8.wireOp",EDGE,"E28")])],"isStart":true})]}),makeQuery(id+"F11.opExtrude","CAP_FACE",FACE,{"disambiguationData":[OSD([sQuery(id+"F10.wireOp",EDGE,"E29.bottom"),sQuery(id+"F10.wireOp",EDGE,"E29.top"),sQuery(id+"F10.wireOp",EDGE,"E29.left"),sQuery(id+"F10.wireOp",EDGE,"E29.right")])],"isStart":true})]});
            var sketch = newSketch(context, id + "F18", { "sketchPlane" : qUnion([Q0])});
            skLineSegment(sketch, "E71.bottom", {"start": v(8223.75, 1200.65) * mm, "end": v(8261.85, 1200.65) * mm});
            skLineSegment(sketch, "E71.top", {"start": v(8223.75, -2965.95) * mm, "end": v(8261.85, -2965.95) * mm});
            skLineSegment(sketch, "E71.left", {"start": v(8223.75, 1200.65) * mm, "end": v(8223.75, -2965.95) * mm});
            skLineSegment(sketch, "E71.right", {"start": v(8261.85, 1200.65) * mm, "end": v(8261.85, -2965.95) * mm});
            skLineSegment(sketch, "E72.1.0.0", {"start": v(8630.15, -2965.95) * mm, "end": v(8668.25, -2965.95) * mm});
            skLineSegment(sketch, "E72.1.0.1", {"start": v(8668.25, 1200.65) * mm, "end": v(8668.25, -2965.95) * mm});
            skLineSegment(sketch, "E72.1.0.2", {"start": v(8630.15, 1200.65) * mm, "end": v(8668.25, 1200.65) * mm});
            skLineSegment(sketch, "E72.1.0.3", {"start": v(8630.15, 1200.65) * mm, "end": v(8630.15, -2965.95) * mm});
            skLineSegment(sketch, "E72.2.0.0", {"start": v(9036.55, -2965.95) * mm, "end": v(9074.65, -2965.95) * mm});
            skLineSegment(sketch, "E72.2.0.1", {"start": v(9074.65, 1200.65) * mm, "end": v(9074.65, -2965.95) * mm});
            skLineSegment(sketch, "E72.2.0.2", {"start": v(9036.55, 1200.65) * mm, "end": v(9074.65, 1200.65) * mm});
            skLineSegment(sketch, "E72.2.0.3", {"start": v(9036.55, 1200.65) * mm, "end": v(9036.55, -2965.95) * mm});
            skLineSegment(sketch, "E72.direction1", {"start": v(8223.75, -2965.95) * mm, "end": v(8630.15, -2965.95) * mm, "construction": true});
            skLineSegment(sketch, "E73.0.3.0", {"start": v(9442.95, -2965.95) * mm, "end": v(9481.05, -2965.95) * mm});
            skLineSegment(sketch, "E73.3.3.0", {"start": v(9481.05, 1200.65) * mm, "end": v(9481.05, -2965.95) * mm});
            skLineSegment(sketch, "E73.6.3.0", {"start": v(9442.95, 1200.65) * mm, "end": v(9481.05, 1200.65) * mm});
            skLineSegment(sketch, "E73.9.3.0", {"start": v(9442.95, 1200.65) * mm, "end": v(9442.95, -2965.95) * mm});
            skLineSegment(sketch, "E73.0.4.0", {"start": v(9849.35, -2965.95) * mm, "end": v(9887.45, -2965.95) * mm});
            skLineSegment(sketch, "E73.3.4.0", {"start": v(9887.45, 1200.65) * mm, "end": v(9887.45, -2965.95) * mm});
            skLineSegment(sketch, "E73.6.4.0", {"start": v(9849.35, 1200.65) * mm, "end": v(9887.45, 1200.65) * mm});
            skLineSegment(sketch, "E73.9.4.0", {"start": v(9849.35, 1200.65) * mm, "end": v(9849.35, -2965.95) * mm});
            skLineSegment(sketch, "E73.0.5.0", {"start": v(10255.75, -2965.95) * mm, "end": v(10293.85, -2965.95) * mm});
            skLineSegment(sketch, "E73.3.5.0", {"start": v(10293.85, 1200.65) * mm, "end": v(10293.85, -2965.95) * mm});
            skLineSegment(sketch, "E73.6.5.0", {"start": v(10255.75, 1200.65) * mm, "end": v(10293.85, 1200.65) * mm});
            skLineSegment(sketch, "E73.9.5.0", {"start": v(10255.75, 1200.65) * mm, "end": v(10255.75, -2965.95) * mm});
            skLineSegment(sketch, "E73.0.6.0", {"start": v(10662.15, -2965.95) * mm, "end": v(10700.25, -2965.95) * mm});
            skLineSegment(sketch, "E73.3.6.0", {"start": v(10700.25, 1200.65) * mm, "end": v(10700.25, -2965.95) * mm});
            skLineSegment(sketch, "E73.6.6.0", {"start": v(10662.15, 1200.65) * mm, "end": v(10700.25, 1200.65) * mm});
            skLineSegment(sketch, "E73.9.6.0", {"start": v(10662.15, 1200.65) * mm, "end": v(10662.15, -2965.95) * mm});
            skLineSegment(sketch, "E73.0.7.0", {"start": v(11068.55, -2965.95) * mm, "end": v(11106.65, -2965.95) * mm});
            skLineSegment(sketch, "E73.3.7.0", {"start": v(11106.65, 1200.65) * mm, "end": v(11106.65, -2965.95) * mm});
            skLineSegment(sketch, "E73.6.7.0", {"start": v(11068.55, 1200.65) * mm, "end": v(11106.65, 1200.65) * mm});
            skLineSegment(sketch, "E73.9.7.0", {"start": v(11068.55, 1200.65) * mm, "end": v(11068.55, -2965.95) * mm});
            skLineSegment(sketch, "E73.0.8.0", {"start": v(11474.95, -2965.95) * mm, "end": v(11513.05, -2965.95) * mm});
            skLineSegment(sketch, "E73.3.8.0", {"start": v(11513.05, 1200.65) * mm, "end": v(11513.05, -2965.95) * mm});
            skLineSegment(sketch, "E73.6.8.0", {"start": v(11474.95, 1200.65) * mm, "end": v(11513.05, 1200.65) * mm});
            skLineSegment(sketch, "E73.9.8.0", {"start": v(11474.95, 1200.65) * mm, "end": v(11474.95, -2965.95) * mm});
            skLineSegment(sketch, "E73.0.9.0", {"start": v(11881.35, -2965.95) * mm, "end": v(11919.45, -2965.95) * mm});
            skLineSegment(sketch, "E73.3.9.0", {"start": v(11919.45, 1200.65) * mm, "end": v(11919.45, -2965.95) * mm});
            skLineSegment(sketch, "E73.6.9.0", {"start": v(11881.35, 1200.65) * mm, "end": v(11919.45, 1200.65) * mm});
            skLineSegment(sketch, "E73.9.9.0", {"start": v(11881.35, 1200.65) * mm, "end": v(11881.35, -2965.95) * mm});
            skSolve(sketch);
        }
        {
            var Q0;
            Q0=qSketchRegion(id+"F18",true);
            var Q1;
            {var subQ3=sQuery(id+"F8.wireOp",EDGE,"E28");var subQ4=sQuery(id+"F8.wireOp",EDGE,"E27");var subQ6=sQuery(id+"F8.wireOp",EDGE,"E26");var subQ7=sQuery(id+"F10.wireOp",EDGE,"E29.left");var subQ8=sQuery(id+"F10.wireOp",EDGE,"E29.top");var subQ9=sQuery(id+"F8.wireOp",EDGE,"E25");var subQ11=sQuery(id+"F10.wireOp",EDGE,"E29.right");var subQ12=sQuery(id+"F8.wireOp",EDGE,"E24");var subQ13=sQuery(id+"F8.wireOp",EDGE,"E23");var subQ14=sQuery(id+"F8.wireOp",EDGE,"E22");Q1=makeQuery(id+"F17.boolean.opBoolean","SPLIT",FACE,{"disambiguationData":[TD([makeQuery(id+"F1.opExtrude","SWEPT_FACE",FACE,{"disambiguationData":[OSD([sQuery(id+"F0.wireOp",EDGE,"E3.bottom")])]})])],"derivedFrom":makeQuery(id+"F11.boolean.opBoolean","MERGE",FACE,{"derivedFrom":[makeQuery(id+"F9.opExtrude","CAP_FACE",FACE,{"disambiguationData":[OSD([subQ14,subQ13,subQ12,subQ9,subQ6,subQ4,subQ3])],"isStart":false}),makeQuery(id+"F11.opExtrude","CAP_FACE",FACE,{"disambiguationData":[OSD([sQuery(id+"F10.wireOp",EDGE,"E29.bottom"),subQ8,subQ7,subQ11])],"isStart":false})]})});}
            extrude(context, id + "F19", {"entities" : qUnion([Q0]), "operationType" : NewBodyOperationType.ADD, "endBound" : BoundingType.UP_TO_SURFACE, "oppositeDirection" : true, "depth" : 25.4 * mm, "endBoundEntityFace" : qUnion([Q1]), "offsetDistance" : 25.4 * mm});
        }
    });
